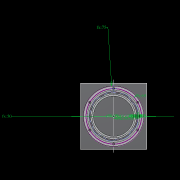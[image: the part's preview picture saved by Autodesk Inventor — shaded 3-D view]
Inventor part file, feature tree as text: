
AUTODESK INVENTOR PART (.ipt)
format: ipt  version: 2022.2 (Build 262287010, 287A)  size: 589,824 bytes
history: native  units: mm
features: other x19, extrude x19, sketch x12, pattern_circular x9, plane x3, fillet x2, move_body x2, revolve x2, draft x2, chamfer x2
ambient origin geometry x8: Origin, YZ Plane, XZ Plane, XY Plane, X Axis, Y Axis, Z Axis, Center Point
bodies: Solid5 (feature_tree)
feature tree (72):
  other  "CrossSection1"
  sketch  "Sketch7"  dims[d90=61.984365mm]
  other  "Roller1"
  other  "Roller2"
  sketch  "Sketch22"  dims[d167=8.972256mm]
  sketch  "Sketch2"  dims[d57=4.025mm]
  sketch  "Sketch23"  dims[d173=10.814812mm]
  other  "RevRoller1"
  fillet  "Fillet1"  Radius=59.246882mm
  pattern_circular  "Circular Pattern13"  Count=360  [1 undecoded]
  move_body  "Move Body7"
  revolve  "Revolution13"  [1 undecoded]
  fillet  "Fillet3"  Radius=0.025mm
  pattern_circular  "Circular Pattern14"  [2 undecoded]
  move_body  "Move Body6"
  revolve  "Revolution14"  [1 undecoded]
  other  "OuterRim_Top2"
  other  "OuterRim_Bottom2"
  plane  "Work Plane7"
  sketch  "Sketch47"  dims[d349=47.575591mm]
  sketch  "Sketch48"  dims[d350=47.575427mm]
  extrude  "Extrusion39"  Depth=2.593516mm
  extrude  "Extrusion40"  Depth=2.593516mm
  pattern_circular  "Circular Pattern28"  Angle=360.0deg  [1 undecoded]
  sketch  "Sketch49"  dims[d351=0.025mm d352=0.025mm d354=0.1mm d355=16.1595mm d356=16.159664mm d358=360.0deg d359=0.5mm d360=240.0mm d361=360.0deg d363=1.308997mm d367=8.1mm d370=0.1mm d371=1.0mm d372=1.308997mm d373=90.0deg d374=0.5mm d375=240.0mm d376=360.0deg d378=90.0deg d379=0.1mm d380=0.1mm d381=0.1mm d382=0.1mm d383=0.1mm d384=11.193516mm d385=0.0mm d386=0.0mm d391=50.0mm d392=75.0mm d393=1.5mm d394=1.5mm d395=1.5mm d396=1.5mm d397=90.0deg d398=90.0deg d399=90.0deg d400=75.0mm d401=11.193516mm d402=0.0mm d486=0.436332mm d487=0.5mm d488=2.0mm d489=0.0mm d490=20.0mm d495=2.5mm d496=8.0mm d506=13.856406mm d507=55.5mm d508=8.0mm d509=0.05mm d510=2.5mm d511=30.0deg d512=12.0mm d513=6.0mm d514=0.2mm d515=30.0deg d516=131.0mm d517=65.5mm d518=0.2mm d519=100.0mm d520=120.0mm d521=2.0mm d522=150.0mm d530=50.0mm d531=5.5mm d532=5.5mm d533=5.5mm d534=85.75mm d535=73.5mm d536=61.25mm d537=24.5mm d538=3.0mm d539=2.4mm d540=0.0mm d541=0.0mm d542=0.0mm d543=5.5mm d544=3.0mm d545=0.0mm d546=90.0mm d547=360.0deg d549=3.0mm d550=3.0mm d551=2.4mm d552=0.0mm d553=5.596758mm d554=0.0mm d555=2.4mm d556=0.0mm d557=5.596758mm d558=0.0mm d559=5.596758mm d560=0.0mm d561=90.0mm d562=360.0deg d564=60.0mm d565=360.0deg d567=5.5mm d568=5.5mm d569=3.0mm d570=0.0mm d571=5.596758mm d572=0.0mm d573=3.0mm d574=0.0mm d575=5.596758mm d576=0.0mm d577=90.0mm d578=360.0deg d580=60.0mm d581=360.0deg d584=20.0mm d585=8.0mm d587=1.75mm d589=3.0mm d592=2.0mm d593=12.0mm d594=12.0mm d600=0.5mm d601=2.0mm d602=45.0deg d603=0.5mm d604=2.0mm d605=45.0deg d606=0.436332mm d607=0.5mm d608=0.0mm d609=20.0mm d611=360.0deg d613=0.0mm d614=0.0mm d617=0.99971mm d618=100.0mm d620=69.0mm d621=3.0mm d622=5.5mm d623=5.596758mm d624=0.0mm d625=3.0mm d626=0.0mm d627=60.0mm d628=360.0deg d630=5.5mm d631=3.0mm d632=5.596758mm d633=0.0mm d634=2.593516mm d635=0.0mm d636=60.0mm d637=360.0deg d16=0.872665mm d17=0.872665mm d49=0.872665mm d50=0.872665mm d51=0.872665mm d52=0.872665mm d236=0.5mm d237=0.872665mm d238=0.5mm d239=0.872665mm d282=1.0mm d283=1.0mm d284=1.0mm d285=0.15mm d286=0.25mm d287=0.375mm d288=14.3117mm d289=0.75mm d290=20.594885mm d291=0.0625mm d292=0.75mm d293=0.375mm d405=0.5mm d406=0.872665mm d407=0.5mm d408=0.872665mm d413=0.5mm d414=0.872665mm d415=0.5mm d416=0.872665mm d417=0.5mm d418=0.872665mm d419=0.5mm d420=0.872665mm d421=0.872665mm d431=0.5mm d432=0.872665mm d433=0.5mm d434=0.872665mm d471=0.5mm d472=0.872665mm d473=0.5mm d474=0.872665mm d497=0.5mm d498=0.872665mm d499=0.5mm d500=0.872665mm d590=0.5mm d591=0.872665mm]
  extrude  "Extrusion41"  Depth=2.593516mm
  extrude  "Extrusion42"  Depth=2.593516mm
  pattern_circular  "Circular Pattern29"  Angle=360.0deg  [1 undecoded]
  extrude  "Rotor_Ring"  Depth=2.593516mm
  draft  "FaceDraft2"
  sketch  "Sketch30"  dims[d201=75.0mm d232=0.0mm d233=3600.0mm]
  plane  "Work Plane5"
  other  "Rotor Featurs"
  other  "RotorRim_Bottom"
  extrude  "Extrusion24"  Depth=2.593516mm
  extrude  "Extrusion25"  Depth=0.1mm
  extrude  "Extrusion26"  Depth=2.593516mm
  pattern_circular  "Circular Pattern23"  [2 undecoded]
  sketch  "Sketch41"  dims[d346=0.025mm]
  extrude  "Extrusion27"  TaperAngle=90.0deg  [1 undecoded]
  extrude  "Extrusion28"  Depth=2.593516mm
  pattern_circular  "Circular Pattern24"  Count=24  [1 undecoded]
  extrude  "Extrusion29"  TaperAngle=360.0deg  [1 undecoded]
  extrude  "Extrusion30"  TaperAngle=90.0deg  [1 undecoded]
  extrude  "Extrusion31"  Depth=0.1mm
  pattern_circular  "Circular Pattern25"  [2 undecoded]
  sketch  "Sketch42"  dims[d347=0.1mm]
  extrude  "Extrusion32"  Depth=0.1mm
  extrude  "Extrusion33"  Depth=0.1mm
  extrude  "Extrusion34"  Depth=0.1mm
  extrude  "Extrusion35"  Depth=11.193516mm
  pattern_circular  "Circular Pattern26"  [2 undecoded]
  pattern_circular  "Circular Pattern27"  [2 undecoded]
  chamfer  "Chamfer1"  Distance=50.0mm
  chamfer  "Chamfer2"  Distance=75.0mm
  draft  "FaceDraft4"
  plane  "Work Plane6"
  sketch  "Sketch43"  dims[d348=0.1mm]
  extrude  "Extrusion37"  Depth=1.5mm
  extrude  "Extrusion38"  Depth=1.5mm
  other  "2D Equation Curve1"
  sketch  "Sketch40"  dims[d343=16.1595mm d344=16.159664mm d345=0.025mm]
  other  "Work Axis6"
  other  "Work Axis7"
  other  "Work Axis8"
  other  "Work Axis9"
  other  "Work Axis10"
  other  "Work Point1"
  other  "Work Point2"
  other  "Work Point3"
  other  "Work Point4"
  other  "Work Point5"
note: 19 required parameter values undecoded (feature->parameter linkage not recoverable at this tier; creation-order binding heuristic only, values carry confidence <= 0.55)